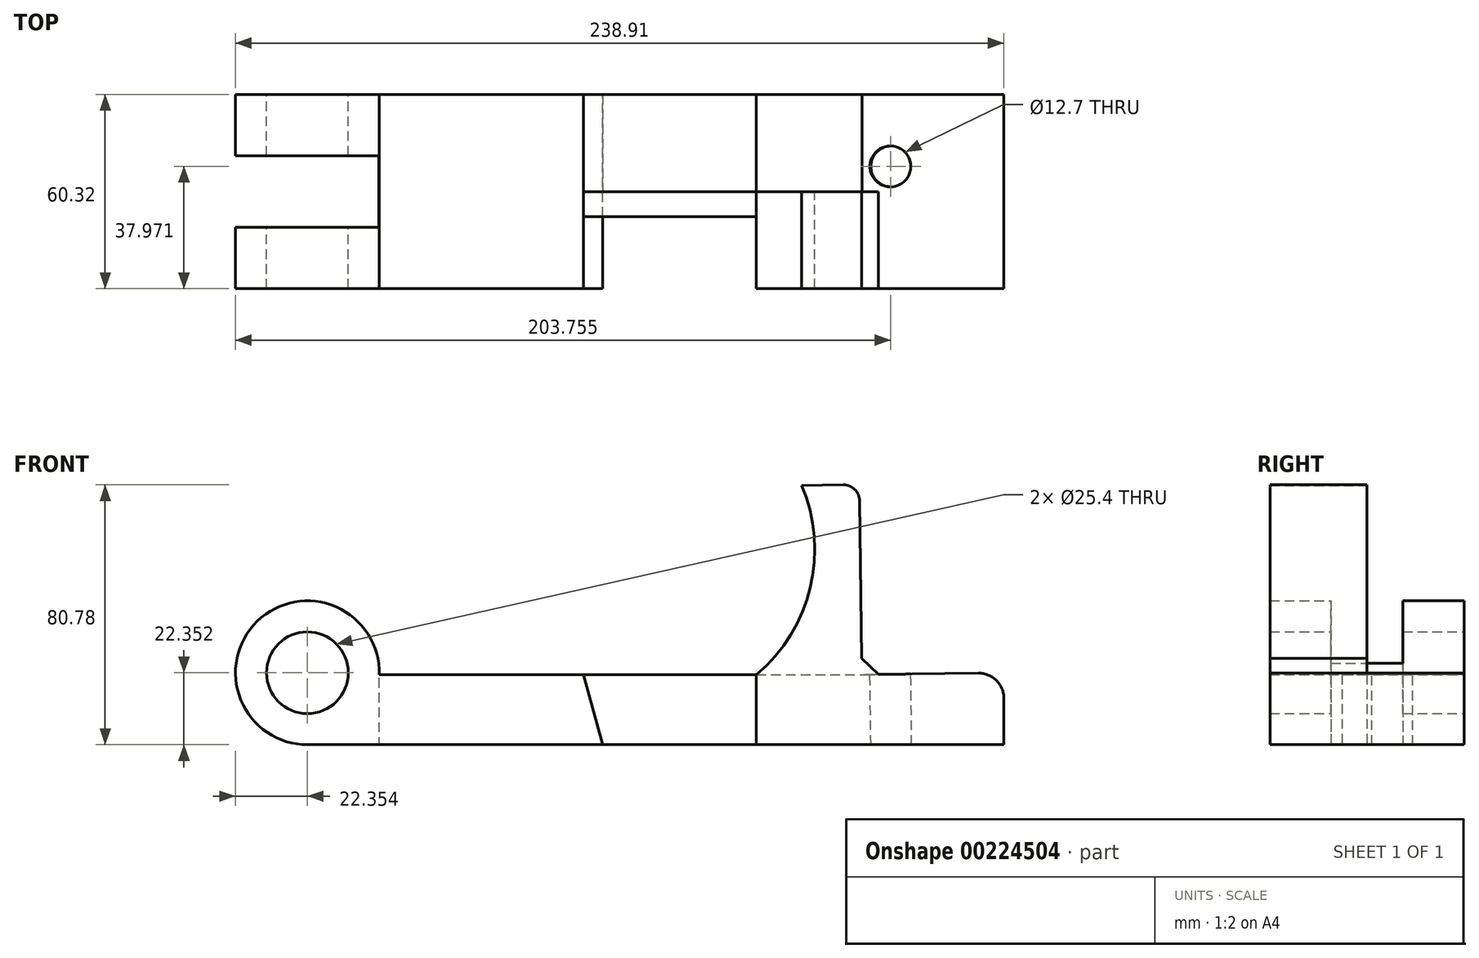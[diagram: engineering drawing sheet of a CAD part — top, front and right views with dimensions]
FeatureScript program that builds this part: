
annotation { "Feature Type Name" : "Feature", "Feature Type Description" : "" }
export const myFeature = defineFeature(function(context is Context, id is Id, definition is map)
    precondition{}
    {
        {
            var Q0;
            Q0=qCreatedBy(makeId("Front.planeOp"),FACE);
            var sketch = newSketch(context, id + "F0", { "sketchPlane" : qUnion([Q0])});
            skLineSegment(sketch, "E0.bottom", {"start": v(0, 0) * mm, "end": v(-91.85, 0) * mm});
            skLineSegment(sketch, "E0.right", {"start": v(-91.85, 0) * mm, "end": v(-91.85, 22.35) * mm});
            skCircle(sketch, "E1", {"center": v(-91.85, 22.35) * mm, "radius": 12.7 * mm});
            skCircle(sketch, "E2", {"center": v(-91.85, 22.35) * mm, "radius": 22.35 * mm});
            skLineSegment(sketch, "E3", {"start": v(0, 0) * mm, "end": v(-6, 21.78) * mm});
            skLineSegment(sketch, "E4", {"start": v(47.75, 21.78) * mm, "end": v(47.75, 0) * mm});
            skLineSegment(sketch, "E5", {"start": v(47.75, 0) * mm, "end": v(0, 0) * mm});
            skLineSegment(sketch, "E6", {"start": v(-6, 21.78) * mm, "end": v(-69.5, 21.78) * mm});
            skLineSegment(sketch, "E7", {"start": v(-6, 21.78) * mm, "end": v(47.75, 21.78) * mm});
            skLineSegment(sketch, "E8", {"start": v(47.75, 0) * mm, "end": v(124.71, 0) * mm});
            skLineSegment(sketch, "E9", {"start": v(124.71, 0) * mm, "end": v(124.71, 22.35) * mm});
            skLineSegment(sketch, "E10", {"start": v(124.71, 22.35) * mm, "end": v(80.6, 21.78) * mm});
            skLineSegment(sketch, "E11", {"start": v(80.6, 21.78) * mm, "end": v(79.83, 80.85) * mm});
            skLineSegment(sketch, "E12", {"start": v(79.83, 80.85) * mm, "end": v(61.83, 80.62) * mm});
            skLineSegment(sketch, "E13", {"start": v(47.75, 21.78) * mm, "end": v(80.6, 21.78) * mm});
            skArc(sketch, "E14", {"start": v(47.75, 21.78) * mm, "mid": v(64.5, 48.87) * mm, "end": v(61.83, 80.62) * mm});
            skSolve(sketch);
        }
        {
            var Q0;
            Q0=makeQuery(id+"F0.imprint","IMPRINT",FACE,{"disambiguationData":[TD([[makeQuery(id+"F0.imprint","IMPRINT",EDGE,{"derivedFrom":sQuery(id+"F0.wireOp",EDGE,"E1")}),-1.0]])]});
            var Q1;
            {var subQ0=sQuery(id+"F0.wireOp",EDGE,"E0.bottom");Q1=makeQuery(id+"F0.imprint","IMPRINT",FACE,{"disambiguationData":[TD([[makeQuery(id+"F0.imprint","IMPRINT",EDGE,{"derivedFrom":subQ0}),-1.0]])]});}
            var Q2;
            Q2=makeQuery(id+"F0.imprint","IMPRINT",FACE,{"disambiguationData":[TD([[makeQuery(id+"F0.imprint","IMPRINT",EDGE,{"derivedFrom":sQuery(id+"F0.wireOp",EDGE,"E4")}),1.0]])]});
            extrude(context, id + "F1", {"entities" : qUnion([Q0, Q1, Q2]), "endBound" : BoundingType.SYMMETRIC, "depth" : 60.32 * mm});
        }
        {
            var Q0;
            Q0=makeQuery(id+"F0.imprint","IMPRINT",FACE,{"disambiguationData":[TD([[makeQuery(id+"F0.imprint","IMPRINT",EDGE,{"derivedFrom":sQuery(id+"F0.wireOp",EDGE,"E11")}),1.0]])]});
            extrude(context, id + "F2", {"entities" : qUnion([Q0]), "operationType" : NewBodyOperationType.ADD, "depth" : 30.16 * mm});
        }
        {
            var Q0;
            Q0=makeQuery(id+"F1.opExtrude","SWEPT_FACE",FACE,{"disambiguationData":[OSD([sQuery(id+"F0.wireOp",EDGE,"E10")])]});
            var sketch = newSketch(context, id + "F3", { "sketchPlane" : qUnion([Q0])});
            skLineSegment(sketch, "E15", {"start": v(125, 30.16) * mm, "end": v(89.69, 30.16) * mm});
            skLineSegment(sketch, "E16", {"start": v(89.69, 30.16) * mm, "end": v(89.69, 7.81) * mm});
            skCircle(sketch, "E17", {"center": v(89.69, 7.81) * mm, "radius": 6.35 * mm});
            skSolve(sketch);
        }
        {
            var Q0;
            Q0=makeQuery(id+"F3.imprint","IMPRINT",FACE,{"disambiguationData":[TD([[makeQuery(id+"F3.imprint","IMPRINT",EDGE,{"derivedFrom":sQuery(id+"F3.wireOp",EDGE,"E17")}),1.0]])]});
            extrude(context, id + "F4", {"entities" : qUnion([Q0]), "operationType" : NewBodyOperationType.REMOVE, "oppositeDirection" : true, "depth" : 80.77 * mm});
        }
        {
            var Q0;
            Q0=makeQuery(id+"F0.imprint","IMPRINT",FACE,{"disambiguationData":[TD([[makeQuery(id+"F0.imprint","IMPRINT",EDGE,{"derivedFrom":sQuery(id+"F0.wireOp",EDGE,"E1")}),1.0]])]});
            var sketch = newSketch(context, id + "F5", { "sketchPlane" : qUnion([Q0])});
            skLineSegment(sketch, "E18.bottom", {"start": v(-70.27, 57.82) * mm, "end": v(-115.48, 57.82) * mm});
            skLineSegment(sketch, "E19.bottom", {"start": v(-69.7, 45.99) * mm, "end": v(-114.9, 45.99) * mm});
            skLineSegment(sketch, "E19.top", {"start": v(-69.7, -45.99) * mm, "end": v(-114.9, -45.99) * mm});
            skLineSegment(sketch, "E19.left", {"start": v(-69.7, 45.99) * mm, "end": v(-69.7, -45.99) * mm});
            skLineSegment(sketch, "E19.right", {"start": v(-114.9, 45.99) * mm, "end": v(-114.9, -45.99) * mm});
            skPoint(sketch, "E19.middle", {"position": v(-92.3, 0) * mm});
            skSolve(sketch);
        }
        {
            var Q0;
            Q0 = qSketchRegion(id + "F5", true);
            extrude(context, id + "F6", {"entities" : qUnion([Q0]), "operationType" : NewBodyOperationType.REMOVE, "endBound" : BoundingType.SYMMETRIC, "depth" : 22.33 * mm});
        }
        {
            var Q0;
            Q0=makeQuery(id+"F0.imprint","IMPRINT",FACE,{"disambiguationData":[TD([[makeQuery(id+"F0.imprint","IMPRINT",EDGE,{"derivedFrom":sQuery(id+"F0.wireOp",EDGE,"E3")}),-1.0]])]});
            extrude(context, id + "F7", {"entities" : qUnion([Q0]), "oppositeDirection" : true, "depth" : 30.16 * mm});
        }
        {
            var Q0;
            Q0=makeQuery(id+"F0.imprint","IMPRINT",FACE,{"disambiguationData":[TD([[makeQuery(id+"F0.imprint","IMPRINT",EDGE,{"derivedFrom":sQuery(id+"F0.wireOp",EDGE,"E3")}),-1.0]])]});
            extrude(context, id + "F8", {"entities" : qUnion([Q0]), "depth" : 7.8 * mm});
        }
        {
            var Q0;
            Q0=makeQuery(id+"F2.opExtrude","SWEPT_EDGE",EDGE,{"disambiguationData":[OSD([sQuery(id+"F0.wireOp",EDGE,"E11"),sQuery(id+"F0.wireOp",EDGE,"E12")])]});
            fillet(context, id + "F9", {"entities" : qUnion([Q0]), "radius" : 5.08 * mm, "tangentPropagation" : true, "allowEdgeOverflow" : false});
        }
        {
            var Q0;
            Q0=makeQuery(id+"F1.opExtrude","SWEPT_EDGE",EDGE,{"disambiguationData":[OSD([sQuery(id+"F0.wireOp",EDGE,"E9"),sQuery(id+"F0.wireOp",EDGE,"E10")])]});
            fillet(context, id + "F10", {"entities" : qUnion([Q0]), "radius" : 7.87 * mm, "tangentPropagation" : true, "allowEdgeOverflow" : false});
        }
        {
            var Q0;
            {var subQ0=sQuery(id+"F0.wireOp",EDGE,"E13");var subQ1=sQuery(id+"F0.wireOp",EDGE,"E11");var subQ2=sQuery(id+"F0.wireOp",EDGE,"E10");Q0=makeQuery(id+"F2.boolean.opBoolean","MERGE",EDGE,{"derivedFrom":[makeQuery(id+"F1.opExtrude","SWEPT_EDGE",EDGE,{"disambiguationData":[OSD([subQ2,subQ1,subQ0])]}),makeQuery(id+"F2.opExtrude","SWEPT_EDGE",EDGE,{"disambiguationData":[OSD([subQ2,subQ1,subQ0])]})]});}
            chamfer(context, id + "F11", {"entities" : qUnion([Q0]), "width" : 5.08 * mm, "tangentPropagation" : true});
        }
    });
